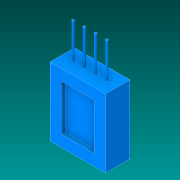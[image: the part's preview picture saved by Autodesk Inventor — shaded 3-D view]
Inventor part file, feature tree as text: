
AUTODESK INVENTOR PART (.ipt)
format: ipt  version: 2019 (Build 230136000, 136)  size: 118,784 bytes
history: native  units: mm
features: sketch x5, extrude x3
ambient origin geometry x8: Origin, YZ Plane, XZ Plane, XY Plane, X Axis, Y Axis, Z Axis, Center Point
bodies: Solid1 (feature_tree)
feature tree (8):
  extrude  "Extrusion1"  Depth=15.5mm
  extrude  "Extrusion3"  Depth=1.0mm TaperAngle=0.0deg
  sketch  "Sketch5"  dims[d49=0.5mm d50=0.5mm]
  sketch  "Sketch7"  dims[d51=0.5mm]
  extrude  "Extrusion4"  Depth=0.5mm
  sketch  "Sketch1"  dims[d0=12.5mm d1=15.5mm]
  sketch  "Sketch3"  dims[d2=5.5mm d3=0.0mm d35=1.0mm d36=0.0mm]
  sketch  "Sketch8"  dims[d52=0.5mm d53=8.0mm d54=0.0mm]
